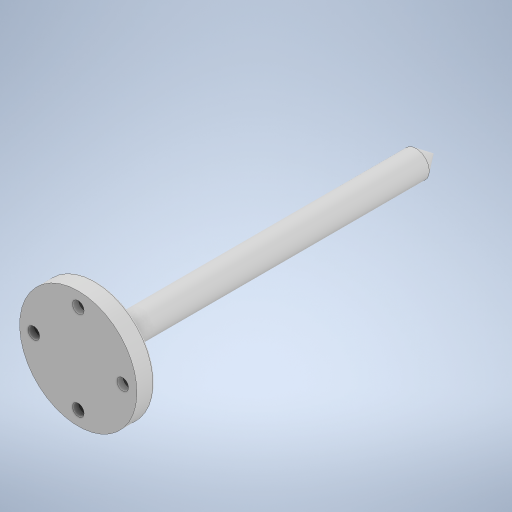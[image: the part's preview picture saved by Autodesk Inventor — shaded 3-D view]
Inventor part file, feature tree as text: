
AUTODESK INVENTOR PART (.ipt)
format: ipt  version: 2023 (Build 270158000, 158)  size: 268,288 bytes
history: native  units: mm
features: fillet x2, sketch x2, other x1, hole x1, chamfer x1
ambient origin geometry x8: Origin, YZ Plane, XZ Plane, XY Plane, X Axis, Y Axis, Z Axis, Center Point
bodies: Body1 (feature_tree)
feature tree (7):
  other  "Rotace2"
  hole  "Díra4"  [1 undecoded]
  chamfer  "Zkosení4"  Distance=10.0mm
  fillet  "Zaoblení12"  Radius=7.5mm
  fillet  "Zaoblení13"  Radius=190.0mm
  sketch  "Náčrt11"
  sketch  "Náčrt12"
note: 1 required parameter value undecoded (feature->parameter linkage not recoverable at this tier; creation-order binding heuristic only, values carry confidence <= 0.55)
